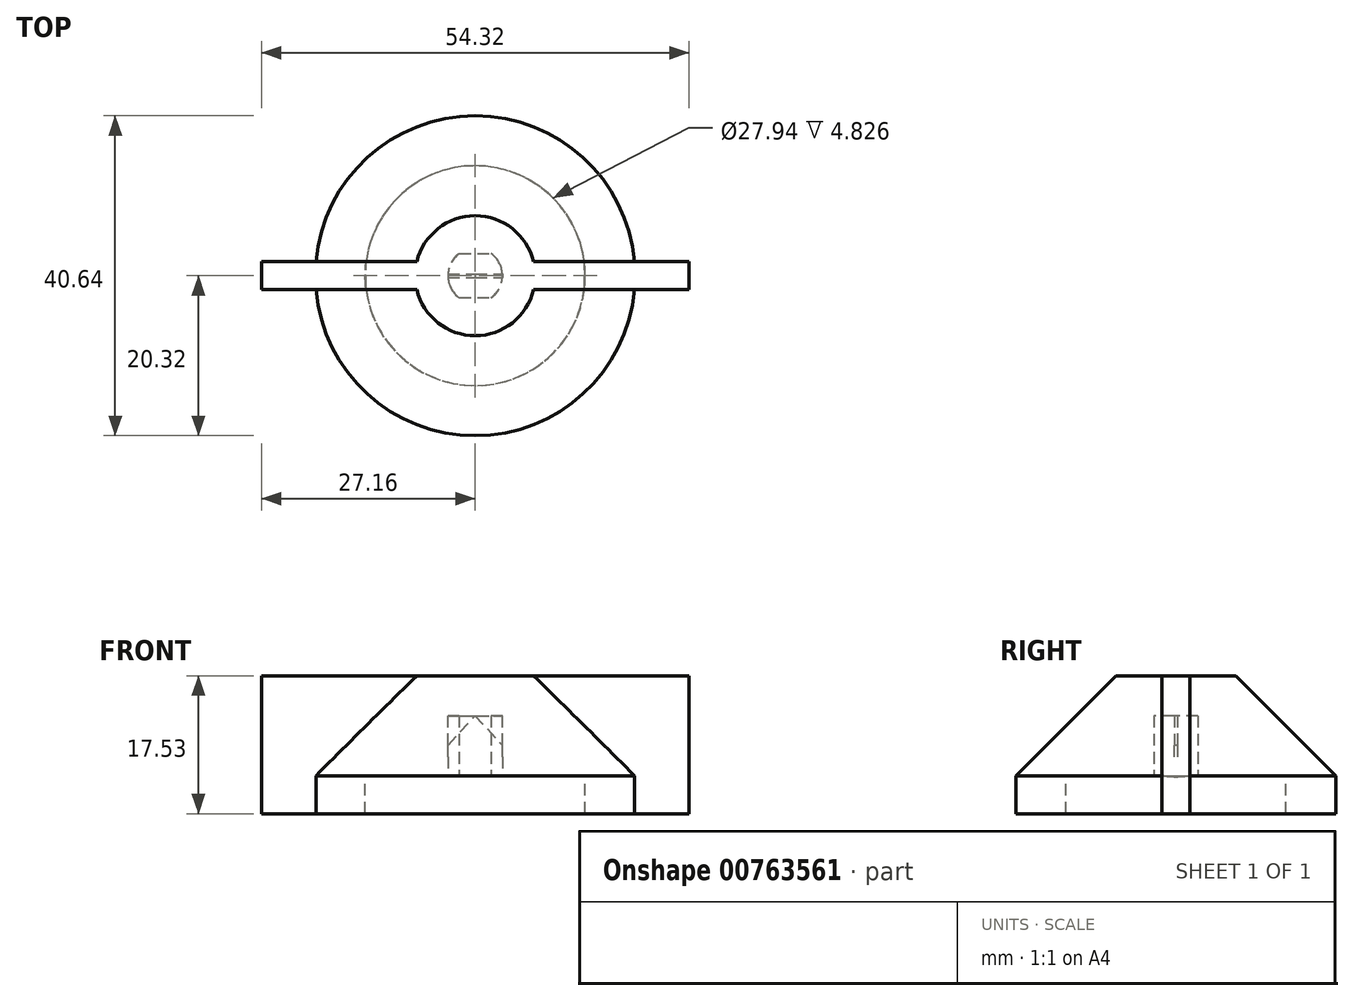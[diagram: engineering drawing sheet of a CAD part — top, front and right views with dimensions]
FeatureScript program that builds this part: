
annotation { "Feature Type Name" : "Feature", "Feature Type Description" : "" }
export const myFeature = defineFeature(function(context is Context, id is Id, definition is map)
    precondition{}
    {
        {
            var Q0;
            Q0=qCreatedBy(makeId("Top.planeOp"),FACE);
            var sketch = newSketch(context, id + "F0", { "sketchPlane" : qUnion([Q0])});
            skCircle(sketch, "E0", {"center": v(0, 0) * mm, "radius": 7.62 * mm});
            skSolve(sketch);
        }
        {
            var Q0;
            Q0 = qSketchRegion(id + "F0", true);
            extrude(context, id + "F1", {"entities" : qUnion([Q0]), "depth" : 12.7 * mm, "offsetDistance" : 25.4 * mm});
        }
        {
            var Q0;
            Q0=qCreatedBy(makeId("Top.planeOp"),FACE);
            var sketch = newSketch(context, id + "F2", { "sketchPlane" : qUnion([Q0])});
            skArc(sketch, "E1", {"start": v(-2.03, 2.8) * mm, "mid": v(-3.46, 0) * mm, "end": v(-2.03, -2.8) * mm});
            skLineSegment(sketch, "E2", {"start": v(-2.03, 2.8) * mm, "end": v(2.03, 2.8) * mm});
            skLineSegment(sketch, "E3.MirrorCS", {"start": v(-2.03, -2.8) * mm, "end": v(2.03, -2.8) * mm});
            skArc(sketch, "E4.trimOffspring", {"start": v(2.03, -2.8) * mm, "mid": v(3.46, 0) * mm, "end": v(2.03, 2.8) * mm});
            skSolve(sketch);
        }
        {
            var Q0;
            Q0 = qSketchRegion(id + "F2", true);
            extrude(context, id + "F3", {"entities" : qUnion([Q0]), "operationType" : NewBodyOperationType.REMOVE, "depth" : 7.62 * mm, "offsetDistance" : 25.4 * mm});
        }
        {
            var Q0;
            Q0=makeQuery(id+"F3.boolean.opBoolean","COPY",FACE,{"derivedFrom":makeQuery(id+"F3.opExtrude","CAP_FACE",FACE,{"disambiguationData":[OSD([sQuery(id+"F2.wireOp",EDGE,"E1"),sQuery(id+"F2.wireOp",EDGE,"E2"),sQuery(id+"F2.wireOp",EDGE,"E3.MirrorCS"),sQuery(id+"F2.wireOp",EDGE,"E4.trimOffspring")])],"isStart":false})});
            var sketch = newSketch(context, id + "F4", { "sketchPlane" : qUnion([Q0])});
            skLineSegment(sketch, "E5.bottom", {"start": v(-3.88, 0) * mm, "end": v(3.93, 0) * mm});
            skLineSegment(sketch, "E5.top", {"start": v(-3.88, -0.22) * mm, "end": v(3.93, -0.22) * mm});
            skLineSegment(sketch, "E5.left", {"start": v(-3.88, 0) * mm, "end": v(-3.88, -0.22) * mm});
            skLineSegment(sketch, "E5.right", {"start": v(3.93, 0) * mm, "end": v(3.93, -0.22) * mm});
            skLineSegment(sketch, "E6.MirrorCS", {"start": v(-3.88, 0.22) * mm, "end": v(3.93, 0.22) * mm});
            skLineSegment(sketch, "E7.MirrorCS", {"start": v(-3.88, 0) * mm, "end": v(-3.88, 0.22) * mm});
            skLineSegment(sketch, "E8.MirrorCS", {"start": v(3.93, 0) * mm, "end": v(3.93, 0.22) * mm});
            skPoint(sketch, "E9", {"position": v(3.46, 0) * mm});
            skSolve(sketch);
        }
        {
            var Q0;
            {var subQ0=sQuery(id+"F4.wireOp",EDGE,"E5.bottom");var subQ1=makeQuery(id+"F3.boolean.opBoolean","COPY",EDGE,{"derivedFrom":makeQuery(id+"F3.opExtrude","CAP_EDGE",EDGE,{"disambiguationData":[OSD([sQuery(id+"F2.wireOp",EDGE,"E1")])],"isStart":false})});var subQ2=makeQuery(id+"F4.imprint","INTERSECT",VERTEX,{"derivedFrom":[subQ1,subQ0]});Q0=makeQuery(id+"F4.imprint","IMPRINT",FACE,{"disambiguationData":[TD([[makeQuery(id+"F4.imprint","IMPRINT",EDGE,{"disambiguationData":[TD([[subQ2,-1.0]])],"derivedFrom":subQ0}),1.0]])]});}
            var Q1;
            {var subQ0=sQuery(id+"F4.wireOp",EDGE,"E5.bottom");var subQ1=makeQuery(id+"F3.boolean.opBoolean","COPY",EDGE,{"derivedFrom":makeQuery(id+"F3.opExtrude","CAP_EDGE",EDGE,{"disambiguationData":[OSD([sQuery(id+"F2.wireOp",EDGE,"E1")])],"isStart":false})});var subQ2=makeQuery(id+"F4.imprint","INTERSECT",VERTEX,{"derivedFrom":[subQ1,subQ0]});Q1=makeQuery(id+"F4.imprint","IMPRINT",FACE,{"disambiguationData":[TD([[makeQuery(id+"F4.imprint","IMPRINT",EDGE,{"disambiguationData":[TD([[subQ2,-1.0]])],"derivedFrom":subQ0}),-1.0]])]});}
            extrude(context, id + "F5", {"entities" : qUnion([Q0, Q1]), "operationType" : NewBodyOperationType.ADD, "depth" : 5.2 * mm, "offsetDistance" : 25.4 * mm});
        }
        {
            var Q0;
            Q0=makeQuery(id+"F5.opExtrude","SWEPT_FACE",FACE,{"disambiguationData":[OSD([sQuery(id+"F4.wireOp",EDGE,"E6.MirrorCS")])]});
            var sketch = newSketch(context, id + "F6", { "sketchPlane" : qUnion([Q0])});
            skLineSegment(sketch, "E10", {"start": v(0, 2.41) * mm, "end": v(0, 7.62) * mm});
            skLineSegment(sketch, "E11", {"start": v(0, 7.62) * mm, "end": v(3.45, 3.87) * mm});
            skLineSegment(sketch, "E12", {"start": v(3.45, 3.87) * mm, "end": v(3.45, 2.41) * mm});
            skLineSegment(sketch, "E13", {"start": v(3.45, 2.41) * mm, "end": v(0, 2.41) * mm});
            skLineSegment(sketch, "E14.MirrorCS", {"start": v(0, 7.62) * mm, "end": v(-3.45, 3.87) * mm});
            skLineSegment(sketch, "E15.MirrorCS", {"start": v(-3.45, 3.87) * mm, "end": v(-3.45, 2.41) * mm});
            skLineSegment(sketch, "E16.MirrorCS", {"start": v(-3.45, 2.41) * mm, "end": v(0, 2.41) * mm});
            skSolve(sketch);
        }
        {
            var Q0;
            Q0=makeQuery(id+"F6.imprint","IMPRINT",FACE,{"disambiguationData":[TD([[makeQuery(id+"F6.imprint","IMPRINT",EDGE,{"derivedFrom":sQuery(id+"F6.wireOp",EDGE,"E10")}),1.0]])]});
            var Q1;
            Q1=makeQuery(id+"F6.imprint","IMPRINT",FACE,{"disambiguationData":[TD([[makeQuery(id+"F6.imprint","IMPRINT",EDGE,{"derivedFrom":sQuery(id+"F6.wireOp",EDGE,"E10")}),-1.0]])]});
            extrude(context, id + "F7", {"entities" : qUnion([Q0, Q1]), "operationType" : NewBodyOperationType.REMOVE, "endBound" : BoundingType.UP_TO_NEXT, "oppositeDirection" : true, "depth" : 25.4 * mm, "offsetDistance" : 25.4 * mm});
        }
        {
            var Q0;
            Q0=qCreatedBy(makeId("Top.planeOp"),FACE);
            var sketch = newSketch(context, id + "F8", { "sketchPlane" : qUnion([Q0])});
            skCircle(sketch, "E17", {"center": v(0, 0) * mm, "radius": 20.32 * mm});
            skSolve(sketch);
        }
        {
            var Q0;
            Q0=makeQuery(id+"F8.imprint","IMPRINT",FACE,{"disambiguationData":[TD([[makeQuery(id+"F8.imprint","IMPRINT",EDGE,{"derivedFrom":sQuery(id+"F8.wireOp",EDGE,"E17")}),1.0]])]});
            extrude(context, id + "F9", {"entities" : qUnion([Q0]), "operationType" : NewBodyOperationType.ADD, "oppositeDirection" : true, "depth" : 4.83 * mm, "offsetDistance" : 25.4 * mm});
        }
        {
            var Q0;
            Q0=makeQuery(id+"F1.opExtrude","CAP_EDGE",EDGE,{"disambiguationData":[OSD([sQuery(id+"F0.wireOp",EDGE,"E0")])],"isStart":true});
            chamfer(context, id + "F10", {"entities" : qUnion([Q0]), "width" : 12.7 * mm, "tangentPropagation" : true});
        }
        {
            var Q0;
            Q0=qCreatedBy(makeId("Top.planeOp"),FACE);
            var sketch = newSketch(context, id + "F11", { "sketchPlane" : qUnion([Q0])});
            skCircle(sketch, "E18", {"center": v(0, 0) * mm, "radius": 13.97 * mm});
            skSolve(sketch);
        }
        {
            var Q0;
            Q0 = qSketchRegion(id + "F11", true);
            extrude(context, id + "F12", {"entities" : qUnion([Q0]), "operationType" : NewBodyOperationType.REMOVE, "endBound" : BoundingType.UP_TO_NEXT, "oppositeDirection" : true, "depth" : 4.83 * mm, "offsetDistance" : 25.4 * mm});
        }
        {
            var Q0;
            Q0=qCreatedBy(makeId("Front.planeOp"),FACE);
            var sketch = newSketch(context, id + "F13", { "sketchPlane" : qUnion([Q0])});
            skLineSegment(sketch, "E19.0", {"start": v(-7.62, 12.7) * mm, "end": v(7.62, 12.7) * mm});
            skLineSegment(sketch, "E20.0.0", {"start": v(20.32, -4.83) * mm, "end": v(-20.32, -4.83) * mm});
            skLineSegment(sketch, "E21", {"start": v(4.75, 12.7) * mm, "end": v(17.35, -4.83) * mm});
            skLineSegment(sketch, "E22", {"start": v(17.35, -4.83) * mm, "end": v(27.16, -4.83) * mm});
            skLineSegment(sketch, "E23", {"start": v(27.16, -4.83) * mm, "end": v(27.16, 12.7) * mm});
            skLineSegment(sketch, "E24", {"start": v(27.16, 12.7) * mm, "end": v(7.62, 12.7) * mm});
            skLineSegment(sketch, "E25.MirrorCS", {"start": v(-4.75, 12.7) * mm, "end": v(-17.35, -4.83) * mm});
            skLineSegment(sketch, "E26.MirrorCS", {"start": v(-27.16, 12.7) * mm, "end": v(-7.62, 12.7) * mm});
            skLineSegment(sketch, "E27.MirrorCS", {"start": v(-27.16, -4.83) * mm, "end": v(-27.16, 12.7) * mm});
            skLineSegment(sketch, "E28.MirrorCS", {"start": v(-17.35, -4.83) * mm, "end": v(-27.16, -4.83) * mm});
            skSolve(sketch);
        }
        {
            var Q0;
            {var subQ1=sQuery(id+"F13.wireOp",EDGE,"E25.MirrorCS");Q0=makeQuery(id+"F13.imprint","IMPRINT",FACE,{"disambiguationData":[TD([[makeQuery(id+"F13.imprint","IMPRINT",EDGE,{"derivedFrom":subQ1}),-1.0]])]});}
            var Q1;
            {var subQ2=sQuery(id+"F13.wireOp",EDGE,"E21");Q1=makeQuery(id+"F13.imprint","IMPRINT",FACE,{"disambiguationData":[TD([[makeQuery(id+"F13.imprint","IMPRINT",EDGE,{"derivedFrom":subQ2}),1.0]])]});}
            extrude(context, id + "F14", {"entities" : qUnion([Q0, Q1]), "operationType" : NewBodyOperationType.ADD, "depth" : 1.78 * mm, "offsetDistance" : 25.4 * mm, "hasSecondDirection" : true, "secondDirectionOppositeDirection" : true, "secondDirectionDepth" : 1.78 * mm});
        }
    });
